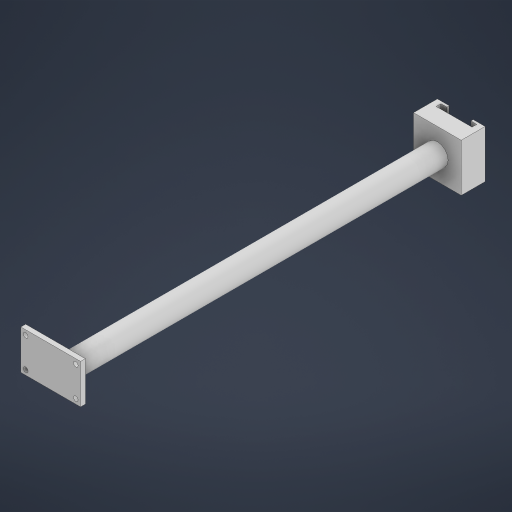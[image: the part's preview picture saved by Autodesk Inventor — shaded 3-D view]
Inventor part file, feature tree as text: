
AUTODESK INVENTOR PART (.ipt)
format: ipt  version: 2024 (Build 280153000, 153)  size: 530,944 bytes
history: native  units: mm
features: extrude x5, sketch x4, other x1
ambient origin geometry x8: Origin, YZ Plane, XZ Plane, XY Plane, X Axis, Y Axis, Z Axis, Center Point
bodies: Body1 (feature_tree)
feature tree (10):
  other  "솔리드1"
  sketch  "스케치1"
  extrude  "돌출1"  Depth=25.0mm
  extrude  "돌출2"  Depth=16.5mm
  extrude  "돌출3"  Depth=2.0mm
  extrude  "돌출4"  Depth=2.0mm
  extrude  "돌출5"  Depth=2.0mm
  sketch  "스케치2"
  sketch  "스케치3"
  sketch  "스케치4"
